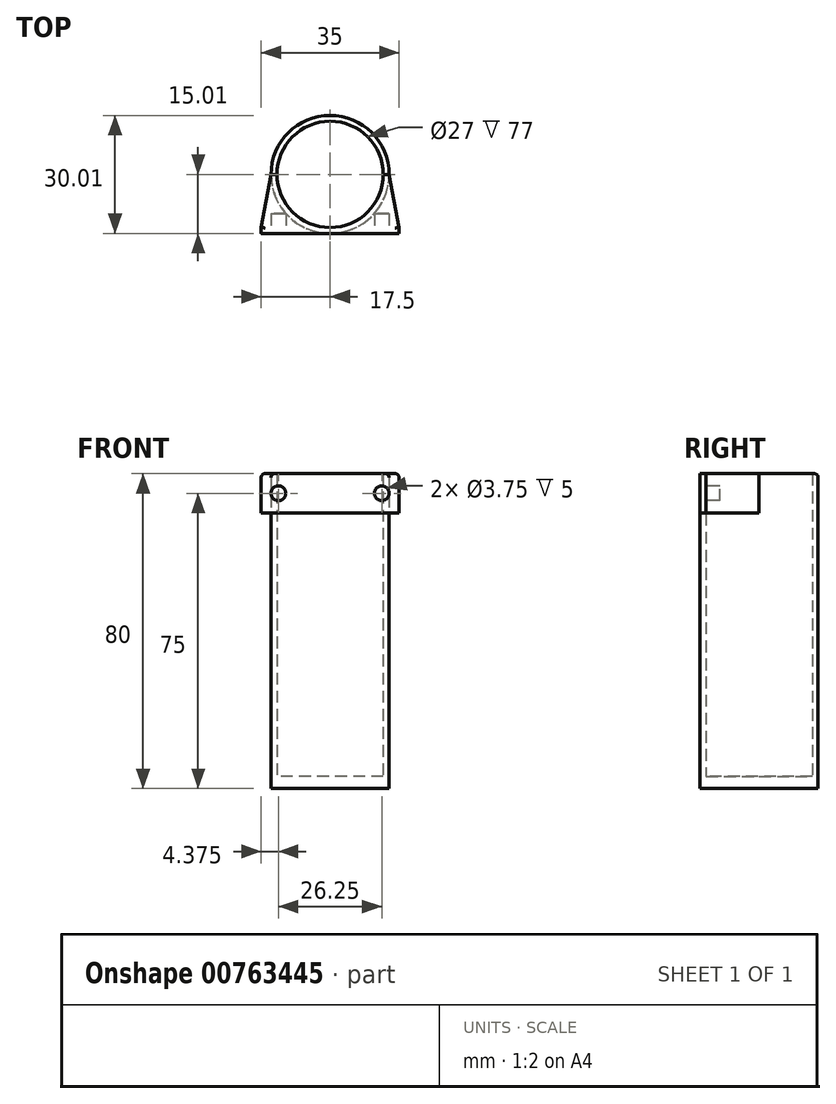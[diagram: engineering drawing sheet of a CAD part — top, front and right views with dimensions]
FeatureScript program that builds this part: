
annotation { "Feature Type Name" : "Feature", "Feature Type Description" : "" }
export const myFeature = defineFeature(function(context is Context, id is Id, definition is map)
    precondition{}
    {
        {
            var Q0;
            Q0=qCreatedBy(makeId("Top.planeOp"),FACE);
            var sketch = newSketch(context, id + "F0", { "sketchPlane" : qUnion([Q0])});
            skCircle(sketch, "E0", {"center": v(0, 0) * mm, "radius": 15 * mm});
            skCircle(sketch, "E1", {"center": v(0, 0) * mm, "radius": 13.5 * mm});
            skLineSegment(sketch, "E2.bottom", {"start": v(17.5, -13.5) * mm, "end": v(-17.5, -13.5) * mm});
            skLineSegment(sketch, "E2.top", {"start": v(17.5, -15) * mm, "end": v(-17.5, -15) * mm});
            skLineSegment(sketch, "E2.left", {"start": v(17.5, -13.5) * mm, "end": v(17.5, -15) * mm});
            skLineSegment(sketch, "E2.right", {"start": v(-17.5, -13.5) * mm, "end": v(-17.5, -15) * mm});
            skPoint(sketch, "E2.middle", {"position": v(0, -14.26) * mm});
            skLineSegment(sketch, "E3", {"start": v(-17.5, -13.5) * mm, "end": v(-15, 0) * mm});
            skLineSegment(sketch, "E4", {"start": v(17.5, -13.5) * mm, "end": v(15, 0) * mm});
            skSolve(sketch);
        }
        {
            var Q0;
            Q0=makeQuery(id+"F0.imprint","IMPRINT",FACE,{"disambiguationData":[TD([[makeQuery(id+"F0.imprint","IMPRINT",EDGE,{"derivedFrom":sQuery(id+"F0.wireOp",EDGE,"E1")}),-1.0]])]});
            var Q1;
            Q1=makeQuery(id+"F0.imprint","IMPRINT",FACE,{"disambiguationData":[TD([[makeQuery(id+"F0.imprint","IMPRINT",EDGE,{"derivedFrom":sQuery(id+"F0.wireOp",EDGE,"E1")}),1.0]])]});
            var Q2;
            {var subQ0=sQuery(id+"F0.wireOp",EDGE,"E2.bottom");var subQ1=sQuery(id+"F0.wireOp",EDGE,"E0");var subQ2=makeQuery(id+"F0.imprint","INTERSECT",VERTEX,{"disambiguationData":[OD(0.0)],"derivedFrom":[subQ1,subQ0]});Q2=makeQuery(id+"F0.imprint","IMPRINT",FACE,{"disambiguationData":[TD([[makeQuery(id+"F0.imprint","IMPRINT",EDGE,{"disambiguationData":[TD([[subQ2,1.0]])],"derivedFrom":subQ1}),1.0]])]});}
            var Q3;
            {var subQ0=sQuery(id+"F0.wireOp",EDGE,"E2.bottom");var subQ1=sQuery(id+"F0.wireOp",EDGE,"E0");var subQ2=makeQuery(id+"F0.imprint","INTERSECT",VERTEX,{"disambiguationData":[OD(0.0)],"derivedFrom":[subQ1,subQ0]});Q3=makeQuery(id+"F0.imprint","IMPRINT",FACE,{"disambiguationData":[TD([[makeQuery(id+"F0.imprint","IMPRINT",EDGE,{"disambiguationData":[TD([[subQ2,-1.0]])],"derivedFrom":subQ1}),1.0]])]});}
            extrude(context, id + "F1", {"entities" : qUnion([Q0, Q1, Q2, Q3]), "depth" : 3 * mm, "offsetDistance" : 25 * mm});
        }
        {
            var Q0;
            Q0=makeQuery(id+"F0.imprint","IMPRINT",FACE,{"disambiguationData":[TD([[makeQuery(id+"F0.imprint","IMPRINT",EDGE,{"derivedFrom":sQuery(id+"F0.wireOp",EDGE,"E2.top")}),-1.0]])]});
            var Q1;
            {var subQ0=sQuery(id+"F0.wireOp",EDGE,"E3");Q1=makeQuery(id+"F0.imprint","IMPRINT",FACE,{"disambiguationData":[TD([[makeQuery(id+"F0.imprint","IMPRINT",EDGE,{"derivedFrom":subQ0}),-1.0]])]});}
            var Q2;
            {var subQ0=sQuery(id+"F0.wireOp",EDGE,"E4");Q2=makeQuery(id+"F0.imprint","IMPRINT",FACE,{"disambiguationData":[TD([[makeQuery(id+"F0.imprint","IMPRINT",EDGE,{"derivedFrom":subQ0}),1.0]])]});}
            var Q3;
            {var subQ0=sQuery(id+"F0.wireOp",EDGE,"E2.bottom");var subQ1=sQuery(id+"F0.wireOp",EDGE,"E0");var subQ2=makeQuery(id+"F0.imprint","INTERSECT",VERTEX,{"disambiguationData":[OD(0.0)],"derivedFrom":[subQ1,subQ0]});Q3=makeQuery(id+"F0.imprint","IMPRINT",FACE,{"disambiguationData":[TD([[makeQuery(id+"F0.imprint","IMPRINT",EDGE,{"disambiguationData":[TD([[subQ2,-1.0]])],"derivedFrom":subQ1}),1.0]])]});}
            var Q4;
            Q4=makeQuery(id+"F0.imprint","IMPRINT",FACE,{"disambiguationData":[TD([[makeQuery(id+"F0.imprint","IMPRINT",EDGE,{"derivedFrom":sQuery(id+"F0.wireOp",EDGE,"E1")}),-1.0]])]});
            extrude(context, id + "F2", {"entities" : qUnion([Q0, Q1, Q2, Q3, Q4]), "operationType" : NewBodyOperationType.ADD, "depth" : 80 * mm, "offsetDistance" : 25 * mm});
        }
        {
            var Q0;
            {var subQ0=sQuery(id+"F0.wireOp",EDGE,"E3");Q0=makeQuery(id+"F0.imprint","IMPRINT",FACE,{"disambiguationData":[TD([[makeQuery(id+"F0.imprint","IMPRINT",EDGE,{"derivedFrom":subQ0}),-1.0]])]});}
            var Q1;
            {var subQ0=sQuery(id+"F0.wireOp",EDGE,"E4");Q1=makeQuery(id+"F0.imprint","IMPRINT",FACE,{"disambiguationData":[TD([[makeQuery(id+"F0.imprint","IMPRINT",EDGE,{"derivedFrom":subQ0}),1.0]])]});}
            var Q2;
            Q2=makeQuery(id+"F0.imprint","IMPRINT",FACE,{"disambiguationData":[TD([[makeQuery(id+"F0.imprint","IMPRINT",EDGE,{"derivedFrom":sQuery(id+"F0.wireOp",EDGE,"E2.top")}),-1.0]])]});
            extrude(context, id + "F3", {"entities" : qUnion([Q0, Q1, Q2]), "operationType" : NewBodyOperationType.REMOVE, "depth" : 70 * mm, "offsetDistance" : 25 * mm});
        }
        {
            var Q0;
            Q0=makeQuery(id+"F2.opExtrude","SWEPT_FACE",FACE,{"disambiguationData":[OSD([sQuery(id+"F0.wireOp",EDGE,"E2.top")])]});
            var sketch = newSketch(context, id + "F4", { "sketchPlane" : qUnion([Q0])});
            skLineSegment(sketch, "E5", {"start": v(0, 70) * mm, "end": v(0, 80) * mm, "construction": true});
            skLineSegment(sketch, "E6", {"start": v(-15, 75) * mm, "end": v(-13.12, 75) * mm, "construction": true});
            skLineSegment(sketch, "E7", {"start": v(15, 75) * mm, "end": v(13.13, 75) * mm, "construction": true});
            skCircle(sketch, "E8", {"center": v(-13.12, 75) * mm, "radius": 1.88 * mm});
            skCircle(sketch, "E9", {"center": v(13.13, 75) * mm, "radius": 1.88 * mm});
            skSolve(sketch);
        }
        {
            var Q0;
            Q0 = qSketchRegion(id + "F4", true);
            extrude(context, id + "F5", {"entities" : qUnion([Q0]), "operationType" : NewBodyOperationType.REMOVE, "oppositeDirection" : true, "depth" : 5 * mm, "offsetDistance" : 25 * mm});
        }
        {
            var Q0;
            Q0=makeQuery(id+"F2.opExtrude","CAP_EDGE",EDGE,{"disambiguationData":[OSD([sQuery(id+"F0.wireOp",EDGE,"E4")])],"isStart":false});
            var Q1;
            Q1=makeQuery(id+"F2.opExtrude","CAP_EDGE",EDGE,{"disambiguationData":[OSD([sQuery(id+"F0.wireOp",EDGE,"E3")])],"isStart":false});
            var Q2;
            Q2=makeQuery(id+"F2.opExtrude","CAP_EDGE",EDGE,{"disambiguationData":[OSD([sQuery(id+"F0.wireOp",EDGE,"E0")])],"isStart":false});
            var Q3;
            Q3=makeQuery(id+"F3.boolean.opBoolean","COPY",EDGE,{"derivedFrom":makeQuery(id+"F3.opExtrude","CAP_EDGE",EDGE,{"disambiguationData":[OSD([sQuery(id+"F0.wireOp",EDGE,"E4")])],"isStart":false})});
            var Q4;
            Q4=makeQuery(id+"F3.boolean.opBoolean","COPY",EDGE,{"derivedFrom":makeQuery(id+"F3.opExtrude","CAP_EDGE",EDGE,{"disambiguationData":[OSD([sQuery(id+"F0.wireOp",EDGE,"E3")])],"isStart":false})});
            var Q5;
            Q5=makeQuery(id+"F2.opExtrude","CAP_EDGE",EDGE,{"disambiguationData":[OSD([sQuery(id+"F0.wireOp",EDGE,"E2.right")])],"isStart":false});
            var Q6;
            Q6=makeQuery(id+"F3.boolean.opBoolean","COPY",EDGE,{"derivedFrom":makeQuery(id+"F3.opExtrude","CAP_EDGE",EDGE,{"disambiguationData":[OSD([sQuery(id+"F0.wireOp",EDGE,"E2.right")])],"isStart":false})});
            var Q7;
            Q7=makeQuery(id+"F2.opExtrude","CAP_EDGE",EDGE,{"disambiguationData":[OSD([sQuery(id+"F0.wireOp",EDGE,"E2.left")])],"isStart":false});
            var Q8;
            Q8=makeQuery(id+"F3.boolean.opBoolean","COPY",EDGE,{"derivedFrom":makeQuery(id+"F3.opExtrude","CAP_EDGE",EDGE,{"disambiguationData":[OSD([sQuery(id+"F0.wireOp",EDGE,"E2.left")])],"isStart":false})});
            var Q9;
            {var subQ0=sQuery(id+"F0.wireOp",EDGE,"E0");Q9=makeQuery(id+"F3.boolean.opBoolean","MERGE",EDGE,{"derivedFrom":[makeQuery(id+"F1.opExtrude","CAP_EDGE",EDGE,{"disambiguationData":[OSD([subQ0])],"isStart":true}),makeQuery(id+"F3.opExtrude","CAP_EDGE",EDGE,{"disambiguationData":[OSD([subQ0])],"isStart":true})]});}
            fillet(context, id + "F6", {"entities" : qUnion([Q0, Q1, Q2, Q3, Q4, Q5, Q6, Q7, Q8, Q9]), "radius" : 1 * mm, "tangentPropagation" : true, "allowEdgeOverflow" : false});
        }
    });
